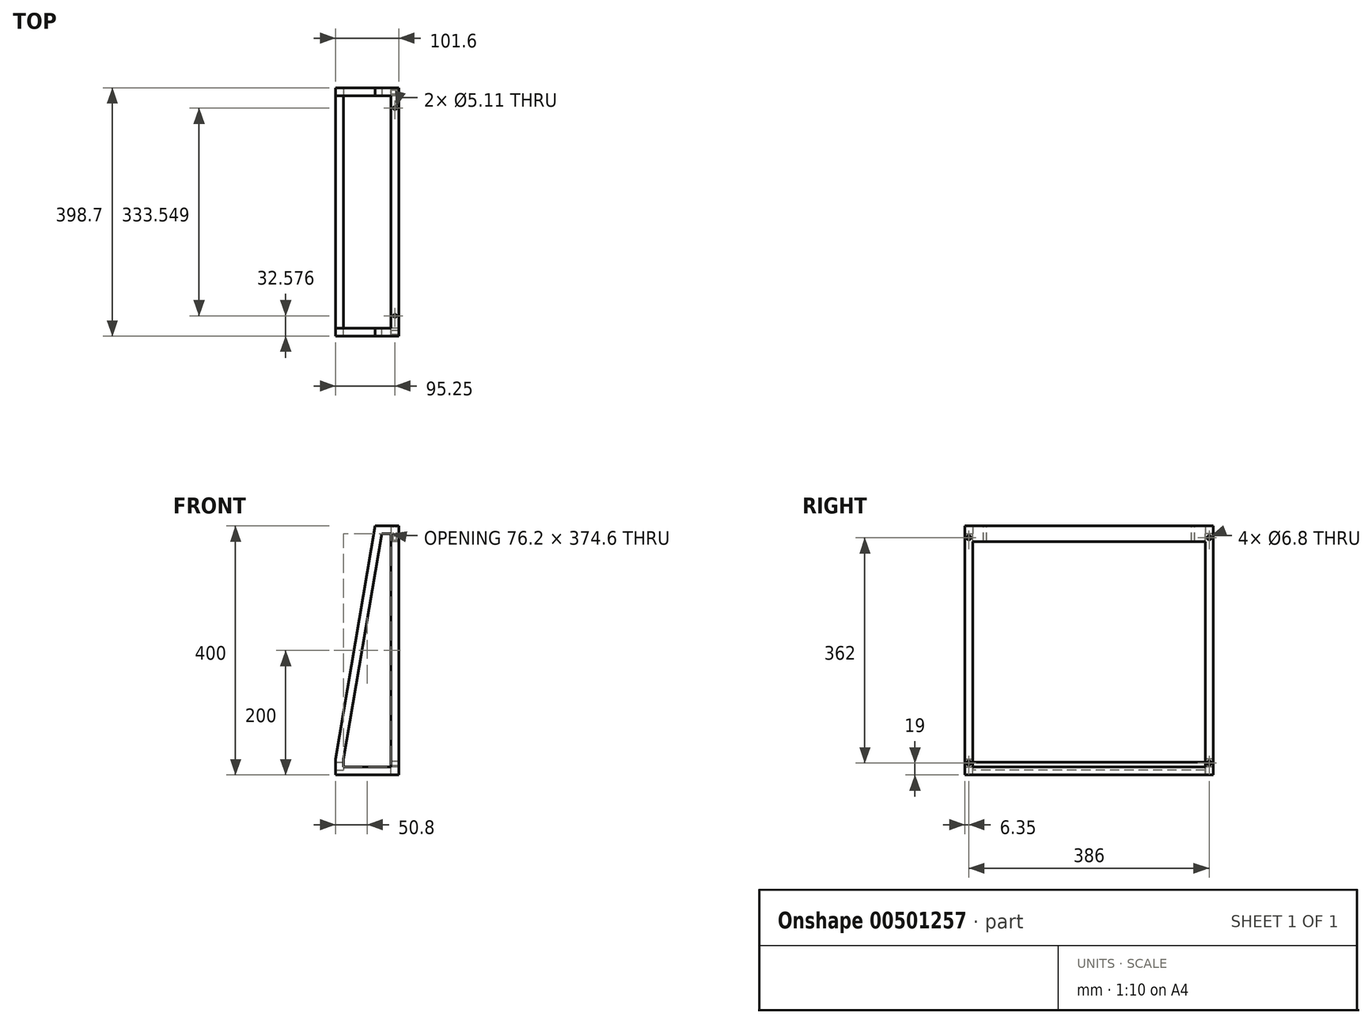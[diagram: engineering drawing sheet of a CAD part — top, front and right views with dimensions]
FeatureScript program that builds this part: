
annotation { "Feature Type Name" : "Feature", "Feature Type Description" : "" }
export const myFeature = defineFeature(function(context is Context, id is Id, definition is map)
    precondition{}
    {
        {
            var Q0;
            Q0=qCreatedBy(makeId("Front.planeOp"),FACE);
            var sketch = newSketch(context, id + "F0", { "sketchPlane" : qUnion([Q0])});
            skLineSegment(sketch, "E0", {"start": v(0, 0) * mm, "end": v(101.6, 0) * mm});
            skLineSegment(sketch, "E1", {"start": v(0, 0) * mm, "end": v(0, 25.4) * mm});
            skLineSegment(sketch, "E2", {"start": v(88.9, 12.7) * mm, "end": v(12.7, 12.7) * mm});
            skPoint(sketch, "E2.endSnap0", {"position": v(0, 12.7) * mm});
            skLineSegment(sketch, "E3", {"start": v(88.9, 387.3) * mm, "end": v(88.9, 12.7) * mm});
            skLineSegment(sketch, "E4", {"start": v(12.7, 25.4) * mm, "end": v(12.7, 12.7) * mm});
            skLineSegment(sketch, "E5", {"start": v(101.6, 0) * mm, "end": v(101.6, 400) * mm});
            skLineSegment(sketch, "E6", {"start": v(101.6, 400) * mm, "end": v(101.6, 387.3) * mm});
            skLineSegment(sketch, "E7", {"start": v(101.6, 400) * mm, "end": v(63.5, 400) * mm});
            skLineSegment(sketch, "E8", {"start": v(63.5, 400) * mm, "end": v(0, 25.4) * mm});
            skLineSegment(sketch, "E9", {"start": v(12.7, 25.4) * mm, "end": v(74.05, 387.3) * mm});
            skLineSegment(sketch, "E10", {"start": v(88.9, 387.3) * mm, "end": v(74.05, 387.3) * mm});
            skSolve(sketch);
        }
        {
            var Q0;
            Q0=makeQuery(id+"F0.imprint","IMPRINT",FACE,{"disambiguationData":[TD([[makeQuery(id+"F0.imprint","IMPRINT",EDGE,{"derivedFrom":sQuery(id+"F0.wireOp",EDGE,"E0")}),1.0]])]});
            extrude(context, id + "F1", {"entities" : qUnion([Q0]), "depth" : 12.7 * mm});
        }
        {
            var Q0;
            Q0=makeQuery(id+"F1.opExtrude","CAP_FACE",FACE,{"disambiguationData":[OSD([sQuery(id+"F0.wireOp",EDGE,"E0"),sQuery(id+"F0.wireOp",EDGE,"E1"),sQuery(id+"F0.wireOp",EDGE,"lfD9ENpA-0lga-AW6R-ttxV-GHqb7ewUG5si"),sQuery(id+"F0.wireOp",EDGE,"E2"),sQuery(id+"F0.wireOp",EDGE,"E3"),sQuery(id+"F0.wireOp",EDGE,"E4"),sQuery(id+"F0.wireOp",EDGE,"IjIzkGph-bBES-M1D0-cM7y-pJEzFIosWM0e"),sQuery(id+"F0.wireOp",EDGE,"E5"),sQuery(id+"F0.wireOp",EDGE,"xkYcUvcZ-cPDE-Xa5v-I4B9-Zc4M6qjwfzsG"),sQuery(id+"F0.wireOp",EDGE,"E6"),sQuery(id+"F0.wireOp",EDGE,"ifux6GjV-N4uH-BMXz-Fh14-0Awf5LUvRzG1")])],"isStart":true});
            var sketch = newSketch(context, id + "F2", { "sketchPlane" : qUnion([Q0])});
            skLineSegment(sketch, "E11.bottom", {"start": v(-101.6, 0) * mm, "end": v(-88.9, 0) * mm});
            skLineSegment(sketch, "E11.top", {"start": v(-101.6, 12.7) * mm, "end": v(-88.9, 12.7) * mm});
            skLineSegment(sketch, "E11.left", {"start": v(-101.6, 0) * mm, "end": v(-101.6, 12.7) * mm});
            skLineSegment(sketch, "E11.right", {"start": v(-88.9, 0) * mm, "end": v(-88.9, 12.7) * mm});
            skLineSegment(sketch, "E12.bottom", {"start": v(-101.6, 400) * mm, "end": v(-88.9, 400) * mm});
            skLineSegment(sketch, "E12.left", {"start": v(-101.6, 400) * mm, "end": v(-101.6, 12.7) * mm});
            skLineSegment(sketch, "E12.right", {"start": v(-88.9, 400) * mm, "end": v(-88.9, 12.7) * mm});
            skLineSegment(sketch, "E13", {"start": v(0, 0) * mm, "end": v(0, 7.87) * mm});
            skLineSegment(sketch, "E14.bottom", {"start": v(0, 7.87) * mm, "end": v(-12.7, 7.87) * mm});
            skLineSegment(sketch, "E14.top", {"start": v(0, 20.57) * mm, "end": v(-12.7, 20.57) * mm});
            skLineSegment(sketch, "E14.left", {"start": v(0, 7.87) * mm, "end": v(0, 20.57) * mm});
            skLineSegment(sketch, "E14.right", {"start": v(-12.7, 7.87) * mm, "end": v(-12.7, 20.57) * mm});
            skLineSegment(sketch, "E15", {"start": v(-101.6, 400) * mm, "end": v(-101.6, 387.3) * mm});
            skLineSegment(sketch, "E16", {"start": v(-101.6, 387.3) * mm, "end": v(-88.9, 387.3) * mm});
            skLineSegment(sketch, "E17", {"start": v(-101.6, 387.3) * mm, "end": v(-101.6, 374.6) * mm});
            skLineSegment(sketch, "E18", {"start": v(-101.6, 374.6) * mm, "end": v(-88.9, 374.6) * mm});
            skLineSegment(sketch, "E19", {"start": v(-88.9, 374.6) * mm, "end": v(-88.9, 387.3) * mm});
            skSolve(sketch);
        }
        {
            var Q0;
            Q0=makeQuery(id+"F2.imprint","IMPRINT",FACE,{"disambiguationData":[TD([[makeQuery(id+"F2.imprint","IMPRINT",EDGE,{"derivedFrom":sQuery(id+"F2.wireOp",EDGE,"E11.bottom")}),-1.0]])]});
            var Q1;
            Q1=makeQuery(id+"F2.imprint","IMPRINT",FACE,{"disambiguationData":[TD([[makeQuery(id+"F2.imprint","IMPRINT",EDGE,{"derivedFrom":sQuery(id+"F2.wireOp",EDGE,"IoMlpHq2-cJgv-B8ZE-quO5-kUIREItqClHN.bottom")}),-1.0]])]});
            var Q2;
            Q2=makeQuery(id+"F2.imprint","IMPRINT",FACE,{"disambiguationData":[TD([[makeQuery(id+"F2.imprint","IMPRINT",EDGE,{"derivedFrom":sQuery(id+"F2.wireOp",EDGE,"E12.bottom")}),-1.0]])]});
            var Q3;
            {var subQ2=sQuery(id+"F2.wireOp",EDGE,"E14.bottom");Q3=makeQuery(id+"F2.imprint","IMPRINT",FACE,{"disambiguationData":[TD([[makeQuery(id+"F2.imprint","IMPRINT",EDGE,{"derivedFrom":subQ2}),-1.0]])]});}
            var Q4;
            Q4=makeQuery(id+"F2.imprint","IMPRINT",FACE,{"disambiguationData":[TD([[makeQuery(id+"F2.imprint","IMPRINT",EDGE,{"derivedFrom":sQuery(id+"F2.wireOp",EDGE,"E16")}),-1.0]])]});
            extrude(context, id + "F3", {"entities" : qUnion([Q0, Q1, Q2, Q3, Q4]), "operationType" : NewBodyOperationType.ADD, "depth" : 373.3 * mm});
        }
        {
            var Q0;
            Q0=makeQuery(id+"F3.opExtrude","CAP_FACE",FACE,{"disambiguationData":[OSD([sQuery(id+"F2.wireOp",EDGE,"E12.bottom"),sQuery(id+"F2.wireOp",EDGE,"E11.top"),sQuery(id+"F2.wireOp",EDGE,"E12.left"),sQuery(id+"F2.wireOp",EDGE,"E12.right")])],"isStart":false});
            var sketch = newSketch(context, id + "F4", { "sketchPlane" : qUnion([Q0])});
            skLineSegment(sketch, "E20.1.0", {"start": v(-101.6, 0) * mm, "end": v(-101.6, 400) * mm});
            skLineSegment(sketch, "E20.1.3", {"start": v(0, 25.4) * mm, "end": v(0, 0) * mm});
            skLineSegment(sketch, "E20.1.4", {"start": v(0, 0) * mm, "end": v(-101.6, 0) * mm});
            skLineSegment(sketch, "E21.1", {"start": v(-88.9, 239.3) * mm, "end": v(-82.67, 239.3) * mm});
            skLineSegment(sketch, "E21.2", {"start": v(-88.9, 239.3) * mm, "end": v(-88.9, 12.7) * mm});
            skLineSegment(sketch, "E21.3", {"start": v(-12.7, 25.4) * mm, "end": v(-12.7, 12.7) * mm});
            skLineSegment(sketch, "E21.4", {"start": v(-88.9, 12.7) * mm, "end": v(-12.7, 12.7) * mm});
            skLineSegment(sketch, "E22.0", {"start": v(-88.9, 387.3) * mm, "end": v(-88.9, 12.7) * mm});
            skLineSegment(sketch, "E22.1", {"start": v(-12.7, 25.4) * mm, "end": v(-74.05, 387.3) * mm});
            skLineSegment(sketch, "E22.2", {"start": v(-88.9, 387.3) * mm, "end": v(-74.05, 387.3) * mm});
            skLineSegment(sketch, "E23.0", {"start": v(-63.5, 400) * mm, "end": v(0, 25.4) * mm});
            skLineSegment(sketch, "E23.1", {"start": v(-101.6, 400) * mm, "end": v(-63.5, 400) * mm});
            skSolve(sketch);
        }
        {
            var Q0;
            {var subQ3=makeQuery(id+"F3.opExtrude","CAP_EDGE",EDGE,{"disambiguationData":[OSD([sQuery(id+"F2.wireOp",EDGE,"E11.top")])],"isStart":false});Q0=makeQuery(id+"F4.imprint","IMPRINT",FACE,{"disambiguationData":[TD([[makeQuery(id+"F4.imprint","IMPRINT",EDGE,{"derivedFrom":subQ3}),1.0]])]});}
            var Q1;
            {var subQ5=sQuery(id+"F4.wireOp",EDGE,"E20.1.2");Q1=makeQuery(id+"F4.imprint","IMPRINT",FACE,{"disambiguationData":[TD([[makeQuery(id+"F4.imprint","IMPRINT",EDGE,{"derivedFrom":subQ5}),-1.0]])]});}
            var Q2;
            Q2=makeQuery(id+"F4.imprint","IMPRINT",FACE,{"disambiguationData":[TD([[makeQuery(id+"F4.imprint","IMPRINT",EDGE,{"derivedFrom":sQuery(id+"F4.wireOp",EDGE,"E20.1.3")}),-1.0]])]});
            var Q3;
            {var subQ4=makeQuery(id+"F3.opExtrude","CAP_EDGE",EDGE,{"disambiguationData":[OSD([sQuery(id+"F2.wireOp",EDGE,"E12.right")])],"isStart":false});Q3=makeQuery(id+"F4.imprint","IMPRINT",FACE,{"disambiguationData":[TD([[makeQuery(id+"F4.imprint","IMPRINT",EDGE,{"derivedFrom":subQ4}),-1.0]])]});}
            extrude(context, id + "F5", {"entities" : qUnion([Q0, Q1, Q2, Q3]), "operationType" : NewBodyOperationType.ADD, "depth" : 12.7 * mm});
        }
        {
            var Q0;
            Q0=makeQuery(id+"F5.boolean.opBoolean","MERGE",FACE,{"derivedFrom":[makeQuery(id+"F3.boolean.opBoolean","MERGE",FACE,{"derivedFrom":[makeQuery(id+"F1.opExtrude","SWEPT_FACE",FACE,{"disambiguationData":[OSD([sQuery(id+"F0.wireOp",EDGE,"E5"),sQuery(id+"F0.wireOp",EDGE,"E6")])]}),makeQuery(id+"F3.opExtrude","SWEPT_FACE",FACE,{"disambiguationData":[OSD([sQuery(id+"F2.wireOp",EDGE,"E11.left")])]}),makeQuery(id+"F3.opExtrude","SWEPT_FACE",FACE,{"disambiguationData":[OSD([sQuery(id+"F2.wireOp",EDGE,"E12.left")])]})]}),makeQuery(id+"F5.opExtrude","SWEPT_FACE",FACE,{"disambiguationData":[OSD([sQuery(id+"F4.wireOp",EDGE,"E20.1.0")])]})]});
            var sketch = newSketch(context, id + "F6", { "sketchPlane" : qUnion([Q0])});
            skLineSegment(sketch, "E24", {"start": v(-12.7, 0) * mm, "end": v(-6.35, 0) * mm});
            skLineSegment(sketch, "E25", {"start": v(-6.35, 0) * mm, "end": v(-6.35, 19) * mm});
            skPoint(sketch, "E26.endSnap0", {"position": v(0, 193.65) * mm});
            skLineSegment(sketch, "E27", {"start": v(-6.35, 19) * mm, "end": v(-6.35, 381) * mm});
            skLineSegment(sketch, "E28", {"start": v(186.65, 0) * mm, "end": v(186.65, 83.29) * mm});
            skLineSegment(sketch, "E29.MirrorCS", {"start": v(379.65, 19) * mm, "end": v(379.65, 381) * mm});
            skSolve(sketch);
        }
        {
            var Q0;
            Q0=sQuery(id+"F6.wireOp",VERTEX,"301810f4-b5b0-48fe-9fed-440b1d064d410.MirrorCS.end");
            var Q1;
            Q1=sQuery(id+"F6.wireOp",VERTEX,"60cd97af-2dfd-4b1e-9da8-f66463ed67490.MirrorCS.end");
            var Q2;
            Q2=sQuery(id+"F6.wireOp",VERTEX,"E25.end");
            var Q3;
            Q3=sQuery(id+"F6.wireOp",VERTEX,"c38dfc3b-03b4-4e9e-9462-be59b06b3c6f0.MirrorCS.end");
            var Q4;
            Q4=sQuery(id+"F6.wireOp",VERTEX,"E27.end");
            var Q5;
            Q5=sQuery(id+"F6.wireOp",VERTEX,"E29.MirrorCS.end");
            var Q6;
            Q6=sQuery(id+"F6.wireOp",VERTEX,"E29.MirrorCS.start");
            var Q7;
            Q7=makeQuery(id+"F1.opExtrude","SWEPT_BODY",BODY,{"disambiguationData":[OSD([sQuery(id+"F0.wireOp",EDGE,"E0"),sQuery(id+"F0.wireOp",EDGE,"E1"),sQuery(id+"F0.wireOp",EDGE,"lfD9ENpA-0lga-AW6R-ttxV-GHqb7ewUG5si"),sQuery(id+"F0.wireOp",EDGE,"E2"),sQuery(id+"F0.wireOp",EDGE,"E3"),sQuery(id+"F0.wireOp",EDGE,"E4"),sQuery(id+"F0.wireOp",EDGE,"IjIzkGph-bBES-M1D0-cM7y-pJEzFIosWM0e"),sQuery(id+"F0.wireOp",EDGE,"E5"),sQuery(id+"F0.wireOp",EDGE,"xkYcUvcZ-cPDE-Xa5v-I4B9-Zc4M6qjwfzsG"),sQuery(id+"F0.wireOp",EDGE,"E6"),sQuery(id+"F0.wireOp",EDGE,"ifux6GjV-N4uH-BMXz-Fh14-0Awf5LUvRzG1")])]});
            hole(context, id + "F7", {"style" : HoleStyle.SIMPLE, "endStyle" : HoleEndStyle.BLIND, "standardTappedOrClearance" : lookupTablePath({ "standard" : "ISO", "engagement" : "75%", "pitch" : "1.25 mm", "size" : "M8", "type" : "Tapped" }), "standardBlindInLast" : lookupTablePath({ "standard" : "ISO", "engagement" : "75%", "pitch" : "1.25 mm", "size" : "M8", "type" : "Tapped" }), "holeDiameter" : 6.8 * mm, "showTappedDepth" : true, "holeDepth" : 15.75 * mm, "isTappedThrough" : true, "tappedDepth" : 12 * mm, "tapClearance" : 3, "startFromSketch" : true, "locations" : qUnion([Q0, Q1, Q2, Q3, Q4, Q5, Q6]), "scope" : qUnion([Q7]), "majorDiameter" : 8 * mm});
        }
        {
            var Q0;
            Q0=makeQuery(id+"F5.boolean.opBoolean","MERGE",FACE,{"derivedFrom":[makeQuery(id+"F3.boolean.opBoolean","MERGE",FACE,{"derivedFrom":[makeQuery(id+"F1.opExtrude","SWEPT_FACE",FACE,{"disambiguationData":[OSD([sQuery(id+"F0.wireOp",EDGE,"E7")])]}),makeQuery(id+"F3.opExtrude","SWEPT_FACE",FACE,{"disambiguationData":[OSD([sQuery(id+"F2.wireOp",EDGE,"E12.bottom")])]})]}),makeQuery(id+"F5.opExtrude","SWEPT_FACE",FACE,{"disambiguationData":[OSD([sQuery(id+"F4.wireOp",EDGE,"E23.1")])]})]});
            var sketch = newSketch(context, id + "F8", { "sketchPlane" : qUnion([Q0])});
            skLineSegment(sketch, "E30", {"start": v(101.6, 386) * mm, "end": v(101.6, 382.82) * mm});
            skLineSegment(sketch, "E31", {"start": v(101.6, 382.82) * mm, "end": v(101.6, 353.42) * mm});
            skLineSegment(sketch, "E32", {"start": v(101.6, 353.42) * mm, "end": v(95.25, 353.42) * mm});
            skLineSegment(sketch, "E33", {"start": v(101.6, 186.65) * mm, "end": v(70.55, 186.65) * mm});
            skLineSegment(sketch, "E34.MirrorCS", {"start": v(101.6, 19.88) * mm, "end": v(95.25, 19.88) * mm});
            skSolve(sketch);
        }
        {
            var Q0;
            Q0=sQuery(id+"F8.wireOp",VERTEX,"E32.end");
            var Q1;
            Q1=sQuery(id+"F8.wireOp",VERTEX,"E34.MirrorCS.end");
            var Q2;
            Q2=makeQuery(id+"F1.opExtrude","SWEPT_BODY",BODY,{"disambiguationData":[OSD([sQuery(id+"F0.wireOp",EDGE,"E0"),sQuery(id+"F0.wireOp",EDGE,"E1"),sQuery(id+"F0.wireOp",EDGE,"E2"),sQuery(id+"F0.wireOp",EDGE,"E3"),sQuery(id+"F0.wireOp",EDGE,"E4"),sQuery(id+"F0.wireOp",EDGE,"E5"),sQuery(id+"F0.wireOp",EDGE,"E6"),sQuery(id+"F0.wireOp",EDGE,"E7"),sQuery(id+"F0.wireOp",EDGE,"E8"),sQuery(id+"F0.wireOp",EDGE,"E9"),sQuery(id+"F0.wireOp",EDGE,"E10")])]});
            hole(context, id + "F9", {"style" : HoleStyle.SIMPLE, "endStyle" : HoleEndStyle.BLIND, "standardTappedOrClearance" : lookupTablePath({ "standard" : "ANSI", "engagement" : "75%", "pitch" : "20 tpi", "size" : "1/4", "type" : "Tapped" }), "standardBlindInLast" : lookupTablePath({ "standard" : "ANSI", "engagement" : "75%", "pitch" : "20 tpi", "size" : "1/4", "type" : "Tapped" }), "holeDiameter" : 5.1 * mm, "showTappedDepth" : true, "holeDepth" : 30.48 * mm, "isTappedThrough" : true, "tappedDepth" : 26.67 * mm, "tapClearance" : 3, "locations" : qUnion([Q0, Q1]), "scope" : qUnion([Q2]), "majorDiameter" : 6.35 * mm});
        }
    });
